# Revit family: Toilet_Elongated-Right_Height-American_Standard-Cadet_PRO-215FA_Series
name_source: partatom
category: Plumbing Fixtures
revit_build: Autodesk Revit 2014 (Build: 20130308_1515(x64)
units: mm (PartAtom-declared; Revit-internal decimal feet)

## types (2) — shared parameters
ADA Compliant = Yes
Assembly Code = D2010110
Bowl Shape = Elongated
CW Connection = Yes
CWFU = 5
Cold Water Connection Diameter = 1/2"
Cold Water Connection Height = 10"
Cold Water Connection Radius = 1/4"
Cold Water Connection Width = 6"
Default Elevation = 0"
Description = Cadet PRO Right Height Elongated Toilet - White
HW Connection = No
Height = 30 3/8"
Installation Type = Floor Mounted
Length = 28 5/16"
Manufacturer = American Standard
Material = Vitreous China-American Standard-020-White
Price = Prices may vary. Please consult Manufacturer Representative for most up-to-date price list.
Product Documentation Link = https://www.americanstandard-us.com
Product Page URL = https://www.americanstandard-us.com
Revised Date = 01/17/2017
Type Comments = Available Finished White, Bone, Linen
URL = http://www.americanstandard-us.com
Vent Connection = No
WFU = 5
Warranty Information = 5 Years Limited
Waste Connection = Yes
Waste Connection Diameter = 2 1/8"
Waste Connection Radius = 1 1/16"
Width = 18 1/8"
zero-valued in all types: HWFU

## per-type parameters (varying)
| type | Flush Rate |
| 215FA.104 | 1.28gpf (4.8Lpf) |
| 215FA.004 | 1.6gpf (6.0Lpf) |

note: column(s) folded — value = type name in every type: Model

## geometry (parser evidence)
native form markers: Sweep x1
no freeform markers — native parametric forms only
